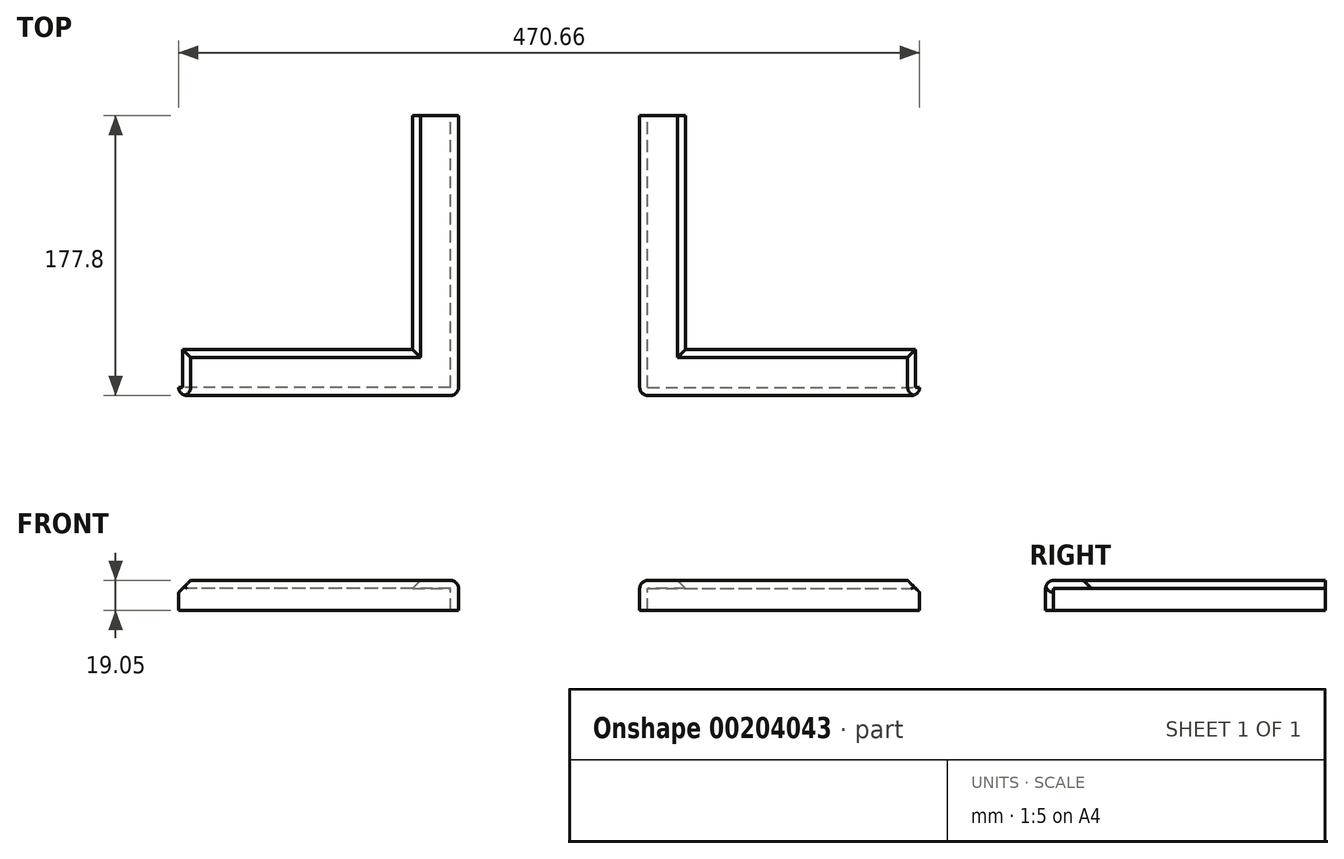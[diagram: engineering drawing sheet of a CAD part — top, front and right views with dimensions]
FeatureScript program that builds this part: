
annotation { "Feature Type Name" : "Feature", "Feature Type Description" : "" }
export const myFeature = defineFeature(function(context is Context, id is Id, definition is map)
    precondition{}
    {
        {
            var Q0;
            Q0=qCreatedBy(makeId("Top.planeOp"),FACE);
            var sketch = newSketch(context, id + "F0", { "sketchPlane" : qUnion([Q0])});
            skLineSegment(sketch, "E0.top", {"start": v(89.28, 0) * mm, "end": v(57.53, 0) * mm});
            skLineSegment(sketch, "E0.left", {"start": v(89.28, -177.8) * mm, "end": v(89.28, 0) * mm});
            skLineSegment(sketch, "E0.right", {"start": v(57.53, -177.8) * mm, "end": v(57.53, 0) * mm});
            skPoint(sketch, "E0.middle", {"position": v(0, 0) * mm});
            skLineSegment(sketch, "E1.bottom", {"start": v(57.53, -177.8) * mm, "end": v(235.33, -177.8) * mm});
            skLineSegment(sketch, "E1.top", {"start": v(57.53, -146.05) * mm, "end": v(235.33, -146.05) * mm});
            skLineSegment(sketch, "E1.right", {"start": v(235.33, -177.8) * mm, "end": v(235.33, -146.05) * mm});
            skSolve(sketch);
        }
        {
            var Q0;
            Q0 = qSketchRegion(id + "F0", true);
            extrude(context, id + "F1", {"entities" : qUnion([Q0]), "oppositeDirection" : true, "depth" : 19.05 * mm});
        }
        {
            var Q0;
            Q0=makeQuery(id+"F1.opExtrude","CAP_FACE",FACE,{"disambiguationData":[OSD([sQuery(id+"F0.wireOp",EDGE,"E0.top"),sQuery(id+"F0.wireOp",EDGE,"E0.left"),sQuery(id+"F0.wireOp",EDGE,"E0.right"),sQuery(id+"F0.wireOp",EDGE,"E1.bottom"),sQuery(id+"F0.wireOp",EDGE,"E1.top"),sQuery(id+"F0.wireOp",EDGE,"E1.left"),sQuery(id+"F0.wireOp",EDGE,"E1.right")])],"isStart":false});
            var Q1;
            Q1=makeQuery(id+"F1.opExtrude","SWEPT_FACE",FACE,{"disambiguationData":[OSD([sQuery(id+"F0.wireOp",EDGE,"E1.top")])]});
            var Q2;
            Q2=makeQuery(id+"F1.opExtrude","SWEPT_FACE",FACE,{"disambiguationData":[OSD([sQuery(id+"F0.wireOp",EDGE,"E0.left")])]});
            var Q3;
            Q3=makeQuery(id+"F1.opExtrude","SWEPT_FACE",FACE,{"disambiguationData":[OSD([sQuery(id+"F0.wireOp",EDGE,"E0.top")])]});
            var Q4;
            Q4=makeQuery(id+"F1.opExtrude","SWEPT_FACE",FACE,{"disambiguationData":[OSD([sQuery(id+"F0.wireOp",EDGE,"E1.right")])]});
            shell(context, id + "F2", {"entities" : qUnion([Q0, Q1, Q2, Q3, Q4]), "thickness" : 5.08 * mm});
        }
        {
            var Q0;
            Q0=makeQuery(id+"F1.opExtrude","CAP_EDGE",EDGE,{"disambiguationData":[OSD([sQuery(id+"F0.wireOp",EDGE,"E0.left")])],"isStart":true});
            var Q1;
            Q1=makeQuery(id+"F1.opExtrude","CAP_EDGE",EDGE,{"disambiguationData":[OSD([sQuery(id+"F0.wireOp",EDGE,"E1.top")])],"isStart":true});
            var Q2;
            Q2=makeQuery(id+"F1.opExtrude","CAP_EDGE",EDGE,{"disambiguationData":[OSD([sQuery(id+"F0.wireOp",EDGE,"E1.right")])],"isStart":true});
            chamfer(context, id + "F3", {"entities" : qUnion([Q0, Q1, Q2]), "width" : 7.62 * mm, "tangentPropagation" : true});
        }
        {
            var Q0;
            Q0=makeQuery(id+"F1.opExtrude","CAP_EDGE",EDGE,{"disambiguationData":[OSD([sQuery(id+"F0.wireOp",EDGE,"E1.bottom")])],"isStart":true});
            var Q1;
            Q1=makeQuery(id+"F1.opExtrude","CAP_EDGE",EDGE,{"disambiguationData":[OSD([sQuery(id+"F0.wireOp",EDGE,"E0.right"),sQuery(id+"F0.wireOp",EDGE,"E1.left")])],"isStart":true});
            fillet(context, id + "F4", {"entities" : qUnion([Q0, Q1]), "radius" : 5.08 * mm, "tangentPropagation" : true, "allowEdgeOverflow" : false});
        }
        {
            var Q0;
            Q0=makeQuery(id+"F1.opExtrude","SWEPT_EDGE",EDGE,{"disambiguationData":[OSD([sQuery(id+"F0.wireOp",EDGE,"E1.bottom"),sQuery(id+"F0.wireOp",EDGE,"E1.left")])]});
            fillet(context, id + "F5", {"entities" : qUnion([Q0]), "radius" : 5.08 * mm, "tangentPropagation" : true, "allowEdgeOverflow" : false});
        }
        {
            var Q0;
            Q0=makeQuery(id+"F1.opExtrude","SWEPT_BODY",BODY,{"disambiguationData":[OSD([sQuery(id+"F0.wireOp",EDGE,"E0.top"),sQuery(id+"F0.wireOp",EDGE,"E0.left"),sQuery(id+"F0.wireOp",EDGE,"E0.right"),sQuery(id+"F0.wireOp",EDGE,"E1.bottom"),sQuery(id+"F0.wireOp",EDGE,"E1.top"),sQuery(id+"F0.wireOp",EDGE,"E1.right")])]});
            var Q1;
            Q1=qCreatedBy(makeId("Right.planeOp"),FACE);
            mirror(context, id + "F6", {"entities" : qUnion([Q0]), "mirrorPlane" : qUnion([Q1])});
        }
    });
